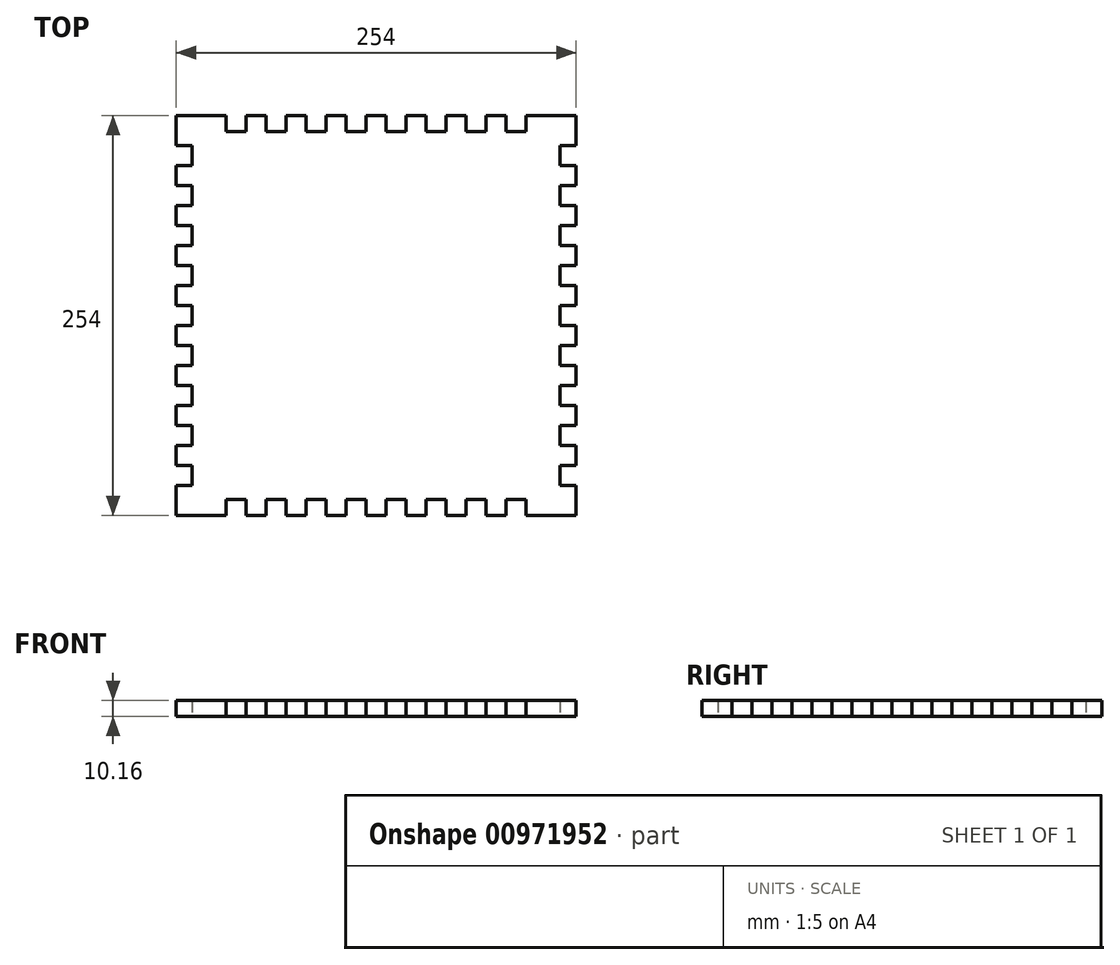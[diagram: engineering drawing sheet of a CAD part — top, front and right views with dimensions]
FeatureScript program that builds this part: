
annotation { "Feature Type Name" : "Feature", "Feature Type Description" : "" }
export const myFeature = defineFeature(function(context is Context, id is Id, definition is map)
    precondition{}
    {
        {
            var Q0;
            Q0=qCreatedBy(makeId("Top.planeOp"),FACE);
            var sketch = newSketch(context, id + "F0", { "sketchPlane" : qUnion([Q0])});
            skLineSegment(sketch, "E0.bottom", {"start": v(0, 0) * mm, "end": v(31.75, 0) * mm});
            skLineSegment(sketch, "E0.left", {"start": v(0, 0) * mm, "end": v(0, -19.05) * mm});
            skLineSegment(sketch, "E1", {"start": v(0, -19.05) * mm, "end": v(10.16, -19.05) * mm});
            skLineSegment(sketch, "E2", {"start": v(10.16, -19.05) * mm, "end": v(10.16, -31.75) * mm});
            skLineSegment(sketch, "E3", {"start": v(10.16, -31.75) * mm, "end": v(0, -31.75) * mm});
            skLineSegment(sketch, "E4", {"start": v(0, -31.75) * mm, "end": v(0, -44.45) * mm});
            skLineSegment(sketch, "E5", {"start": v(0, -44.45) * mm, "end": v(10.16, -44.45) * mm});
            skLineSegment(sketch, "E6", {"start": v(10.16, -44.45) * mm, "end": v(10.16, -57.15) * mm});
            skLineSegment(sketch, "E7", {"start": v(10.16, -57.15) * mm, "end": v(0, -57.15) * mm});
            skLineSegment(sketch, "E8", {"start": v(0, -57.15) * mm, "end": v(0, -69.85) * mm});
            skLineSegment(sketch, "E9", {"start": v(0, -69.85) * mm, "end": v(10.16, -69.85) * mm});
            skLineSegment(sketch, "E10", {"start": v(10.16, -69.85) * mm, "end": v(10.16, -82.55) * mm});
            skLineSegment(sketch, "E11", {"start": v(10.16, -82.55) * mm, "end": v(0, -82.55) * mm});
            skLineSegment(sketch, "E12.trimOffspring", {"start": v(0, -82.55) * mm, "end": v(0, -95.25) * mm});
            skLineSegment(sketch, "E13", {"start": v(0, -95.25) * mm, "end": v(10.16, -95.25) * mm});
            skLineSegment(sketch, "E14", {"start": v(10.16, -95.25) * mm, "end": v(10.16, -107.95) * mm});
            skLineSegment(sketch, "E15", {"start": v(10.16, -107.95) * mm, "end": v(0, -107.95) * mm});
            skLineSegment(sketch, "E16", {"start": v(0, -107.95) * mm, "end": v(0, -120.65) * mm});
            skLineSegment(sketch, "E17", {"start": v(0, -120.65) * mm, "end": v(10.16, -120.65) * mm});
            skLineSegment(sketch, "E18", {"start": v(10.16, -120.65) * mm, "end": v(10.16, -133.35) * mm});
            skLineSegment(sketch, "E19", {"start": v(10.16, -133.35) * mm, "end": v(0, -133.35) * mm});
            skLineSegment(sketch, "E20", {"start": v(0, -133.35) * mm, "end": v(0, -146.05) * mm});
            skLineSegment(sketch, "E21", {"start": v(0, -146.05) * mm, "end": v(10.16, -146.05) * mm});
            skLineSegment(sketch, "E22", {"start": v(10.16, -146.05) * mm, "end": v(10.16, -158.75) * mm});
            skLineSegment(sketch, "E23", {"start": v(10.16, -158.75) * mm, "end": v(0, -158.75) * mm});
            skLineSegment(sketch, "E24.trimOffspring", {"start": v(0, -158.75) * mm, "end": v(0, -171.45) * mm});
            skLineSegment(sketch, "E25", {"start": v(0, -171.45) * mm, "end": v(10.16, -171.45) * mm});
            skLineSegment(sketch, "E26", {"start": v(10.16, -171.45) * mm, "end": v(10.16, -184.15) * mm});
            skLineSegment(sketch, "E27", {"start": v(10.16, -184.15) * mm, "end": v(0, -184.15) * mm});
            skLineSegment(sketch, "E28", {"start": v(0, -184.15) * mm, "end": v(0, -196.85) * mm});
            skLineSegment(sketch, "E29", {"start": v(0, -196.85) * mm, "end": v(10.16, -196.85) * mm});
            skLineSegment(sketch, "E30", {"start": v(10.16, -196.85) * mm, "end": v(10.16, -209.55) * mm});
            skLineSegment(sketch, "E31", {"start": v(10.16, -209.55) * mm, "end": v(0, -209.55) * mm});
            skLineSegment(sketch, "E32", {"start": v(0, -209.55) * mm, "end": v(0, -222.25) * mm});
            skLineSegment(sketch, "E33", {"start": v(0, -222.25) * mm, "end": v(10.16, -222.25) * mm});
            skLineSegment(sketch, "E34", {"start": v(10.16, -222.25) * mm, "end": v(10.16, -234.95) * mm});
            skLineSegment(sketch, "E35", {"start": v(10.16, -234.95) * mm, "end": v(0, -234.95) * mm});
            skLineSegment(sketch, "E36.trimOffspring", {"start": v(0, -234.95) * mm, "end": v(0, -254) * mm});
            skLineSegment(sketch, "E37", {"start": v(31.75, 0) * mm, "end": v(31.75, -10.16) * mm});
            skLineSegment(sketch, "E38", {"start": v(31.75, -10.16) * mm, "end": v(44.45, -10.16) * mm});
            skLineSegment(sketch, "E39", {"start": v(44.45, -10.16) * mm, "end": v(44.45, 0) * mm});
            skLineSegment(sketch, "E40", {"start": v(44.45, 0) * mm, "end": v(57.15, 0) * mm});
            skLineSegment(sketch, "E41", {"start": v(57.15, 0) * mm, "end": v(57.15, -10.16) * mm});
            skLineSegment(sketch, "E42", {"start": v(57.15, -10.16) * mm, "end": v(69.85, -10.16) * mm});
            skLineSegment(sketch, "E43", {"start": v(69.85, -10.16) * mm, "end": v(69.85, 0) * mm});
            skLineSegment(sketch, "E44", {"start": v(69.85, 0) * mm, "end": v(82.55, 0) * mm});
            skLineSegment(sketch, "E45", {"start": v(82.55, 0) * mm, "end": v(82.55, -10.16) * mm});
            skLineSegment(sketch, "E46", {"start": v(82.55, -10.16) * mm, "end": v(95.25, -10.16) * mm});
            skLineSegment(sketch, "E47", {"start": v(95.25, -10.16) * mm, "end": v(95.25, 0) * mm});
            skLineSegment(sketch, "E48.trimOffspring", {"start": v(95.25, 0) * mm, "end": v(107.95, 0) * mm});
            skLineSegment(sketch, "E49", {"start": v(107.95, 0) * mm, "end": v(107.95, -10.16) * mm});
            skLineSegment(sketch, "E50", {"start": v(107.95, -10.16) * mm, "end": v(120.65, -10.16) * mm});
            skLineSegment(sketch, "E51", {"start": v(120.65, -10.16) * mm, "end": v(120.65, 0) * mm});
            skLineSegment(sketch, "E52", {"start": v(120.65, 0) * mm, "end": v(133.35, 0) * mm});
            skLineSegment(sketch, "E53", {"start": v(133.35, 0) * mm, "end": v(133.35, -10.16) * mm});
            skLineSegment(sketch, "E54", {"start": v(133.35, -10.16) * mm, "end": v(146.05, -10.16) * mm});
            skLineSegment(sketch, "E55", {"start": v(146.05, -10.16) * mm, "end": v(146.05, 0) * mm});
            skLineSegment(sketch, "E56", {"start": v(146.05, 0) * mm, "end": v(158.75, 0) * mm});
            skLineSegment(sketch, "E57", {"start": v(158.75, 0) * mm, "end": v(158.75, -10.16) * mm});
            skLineSegment(sketch, "E58", {"start": v(158.75, -10.16) * mm, "end": v(171.45, -10.16) * mm});
            skLineSegment(sketch, "E59", {"start": v(171.45, -10.16) * mm, "end": v(171.45, 0) * mm});
            skLineSegment(sketch, "E60.trimOffspring", {"start": v(171.45, 0) * mm, "end": v(184.15, 0) * mm});
            skLineSegment(sketch, "E61", {"start": v(184.15, 0) * mm, "end": v(184.15, -10.16) * mm});
            skLineSegment(sketch, "E62", {"start": v(184.15, -10.16) * mm, "end": v(196.85, -10.16) * mm});
            skLineSegment(sketch, "E63", {"start": v(196.85, -10.16) * mm, "end": v(196.85, 0) * mm});
            skLineSegment(sketch, "E64", {"start": v(196.85, 0) * mm, "end": v(209.55, 0) * mm});
            skLineSegment(sketch, "E65", {"start": v(209.55, 0) * mm, "end": v(209.55, -10.16) * mm});
            skLineSegment(sketch, "E66", {"start": v(209.55, -10.16) * mm, "end": v(222.25, -10.16) * mm});
            skLineSegment(sketch, "E67", {"start": v(222.25, -10.16) * mm, "end": v(222.25, 0) * mm});
            skLineSegment(sketch, "E68.trimOffspring", {"start": v(222.25, 0) * mm, "end": v(254, 0) * mm});
            skLineSegment(sketch, "E69", {"start": v(127, 0) * mm, "end": v(127, -28.6) * mm, "construction": true});
            skLineSegment(sketch, "E70", {"start": v(10.16, -127) * mm, "end": v(33.98, -127) * mm, "construction": true});
            skLineSegment(sketch, "E71.MirrorCS", {"start": v(254, -133.35) * mm, "end": v(254, -146.05) * mm});
            skLineSegment(sketch, "E72.MirrorCS", {"start": v(254, -82.55) * mm, "end": v(254, -95.25) * mm});
            skLineSegment(sketch, "E73.MirrorCS", {"start": v(254, -184.15) * mm, "end": v(254, -196.85) * mm});
            skLineSegment(sketch, "E74.MirrorCS", {"start": v(254, -158.75) * mm, "end": v(254, -171.45) * mm});
            skLineSegment(sketch, "E75.MirrorCS", {"start": v(254, -31.75) * mm, "end": v(254, -44.45) * mm});
            skLineSegment(sketch, "E76.MirrorCS", {"start": v(254, -209.55) * mm, "end": v(254, -222.25) * mm});
            skLineSegment(sketch, "E77.MirrorCS", {"start": v(254, -57.15) * mm, "end": v(254, -69.85) * mm});
            skLineSegment(sketch, "E78.MirrorCS", {"start": v(254, -107.95) * mm, "end": v(254, -120.65) * mm});
            skLineSegment(sketch, "E79.MirrorCS", {"start": v(243.84, -209.55) * mm, "end": v(254, -209.55) * mm});
            skLineSegment(sketch, "E80.MirrorCS", {"start": v(254, -69.85) * mm, "end": v(243.84, -69.85) * mm});
            skLineSegment(sketch, "E81.MirrorCS", {"start": v(254, -19.05) * mm, "end": v(243.84, -19.05) * mm});
            skLineSegment(sketch, "E82.MirrorCS", {"start": v(243.84, -133.35) * mm, "end": v(254, -133.35) * mm});
            skLineSegment(sketch, "E83.MirrorCS", {"start": v(243.84, -107.95) * mm, "end": v(254, -107.95) * mm});
            skLineSegment(sketch, "E84.MirrorCS", {"start": v(254, -44.45) * mm, "end": v(243.84, -44.45) * mm});
            skLineSegment(sketch, "E85.MirrorCS", {"start": v(243.84, -184.15) * mm, "end": v(254, -184.15) * mm});
            skLineSegment(sketch, "E86.MirrorCS", {"start": v(243.84, -158.75) * mm, "end": v(254, -158.75) * mm});
            skLineSegment(sketch, "E87.MirrorCS", {"start": v(254, -222.25) * mm, "end": v(243.84, -222.25) * mm});
            skLineSegment(sketch, "E88.MirrorCS", {"start": v(254, -196.85) * mm, "end": v(243.84, -196.85) * mm});
            skLineSegment(sketch, "E89.MirrorCS", {"start": v(254, -171.45) * mm, "end": v(243.84, -171.45) * mm});
            skLineSegment(sketch, "E90.MirrorCS", {"start": v(243.84, -31.75) * mm, "end": v(254, -31.75) * mm});
            skLineSegment(sketch, "E91.MirrorCS", {"start": v(254, -146.05) * mm, "end": v(243.84, -146.05) * mm});
            skLineSegment(sketch, "E92.MirrorCS", {"start": v(254, -120.65) * mm, "end": v(243.84, -120.65) * mm});
            skLineSegment(sketch, "E93.MirrorCS", {"start": v(243.84, -82.55) * mm, "end": v(254, -82.55) * mm});
            skLineSegment(sketch, "E94.MirrorCS", {"start": v(243.84, -95.25) * mm, "end": v(243.84, -107.95) * mm});
            skLineSegment(sketch, "E95.MirrorCS", {"start": v(243.84, -234.95) * mm, "end": v(254, -234.95) * mm});
            skLineSegment(sketch, "E96.MirrorCS", {"start": v(243.84, -57.15) * mm, "end": v(254, -57.15) * mm});
            skLineSegment(sketch, "E97.MirrorCS", {"start": v(243.84, -19.05) * mm, "end": v(243.84, -31.75) * mm});
            skLineSegment(sketch, "E98.MirrorCS", {"start": v(243.84, -196.85) * mm, "end": v(243.84, -209.55) * mm});
            skLineSegment(sketch, "E99.MirrorCS", {"start": v(243.84, -146.05) * mm, "end": v(243.84, -158.75) * mm});
            skLineSegment(sketch, "E100.MirrorCS", {"start": v(254, -95.25) * mm, "end": v(243.84, -95.25) * mm});
            skLineSegment(sketch, "E101.MirrorCS", {"start": v(243.84, -69.85) * mm, "end": v(243.84, -82.55) * mm});
            skLineSegment(sketch, "E102.MirrorCS", {"start": v(243.84, -222.25) * mm, "end": v(243.84, -234.95) * mm});
            skLineSegment(sketch, "E103.MirrorCS", {"start": v(243.84, -171.45) * mm, "end": v(243.84, -184.15) * mm});
            skLineSegment(sketch, "E104.MirrorCS", {"start": v(243.84, -120.65) * mm, "end": v(243.84, -133.35) * mm});
            skLineSegment(sketch, "E105.MirrorCS", {"start": v(243.84, -44.45) * mm, "end": v(243.84, -57.15) * mm});
            skLineSegment(sketch, "E106.MirrorCS", {"start": v(254, -234.95) * mm, "end": v(254, -254) * mm});
            skLineSegment(sketch, "E107.MirrorCS", {"start": v(254, 0) * mm, "end": v(254, -19.05) * mm});
            skLineSegment(sketch, "E108.MirrorCS", {"start": v(69.85, -254) * mm, "end": v(82.55, -254) * mm});
            skLineSegment(sketch, "E109.MirrorCS", {"start": v(120.65, -254) * mm, "end": v(133.35, -254) * mm});
            skLineSegment(sketch, "E110.MirrorCS", {"start": v(171.45, -254) * mm, "end": v(184.15, -254) * mm});
            skLineSegment(sketch, "E111.MirrorCS", {"start": v(196.85, -254) * mm, "end": v(209.55, -254) * mm});
            skLineSegment(sketch, "E112.MirrorCS", {"start": v(95.25, -254) * mm, "end": v(107.95, -254) * mm});
            skLineSegment(sketch, "E113.MirrorCS", {"start": v(44.45, -254) * mm, "end": v(57.15, -254) * mm});
            skLineSegment(sketch, "E114.MirrorCS", {"start": v(146.05, -254) * mm, "end": v(158.75, -254) * mm});
            skLineSegment(sketch, "E115.MirrorCS", {"start": v(158.75, -254) * mm, "end": v(158.75, -243.84) * mm});
            skLineSegment(sketch, "E116.MirrorCS", {"start": v(31.75, -254) * mm, "end": v(31.75, -243.84) * mm});
            skLineSegment(sketch, "E117.MirrorCS", {"start": v(95.25, -243.84) * mm, "end": v(95.25, -254) * mm});
            skLineSegment(sketch, "E118.MirrorCS", {"start": v(209.55, -243.84) * mm, "end": v(222.25, -243.84) * mm});
            skLineSegment(sketch, "E119.MirrorCS", {"start": v(82.55, -254) * mm, "end": v(82.55, -243.84) * mm});
            skLineSegment(sketch, "E120.MirrorCS", {"start": v(158.75, -243.84) * mm, "end": v(171.45, -243.84) * mm});
            skLineSegment(sketch, "E121.MirrorCS", {"start": v(31.75, -243.84) * mm, "end": v(44.45, -243.84) * mm});
            skLineSegment(sketch, "E122.MirrorCS", {"start": v(196.85, -243.84) * mm, "end": v(196.85, -254) * mm});
            skLineSegment(sketch, "E123.MirrorCS", {"start": v(57.15, -254) * mm, "end": v(57.15, -243.84) * mm});
            skLineSegment(sketch, "E124.MirrorCS", {"start": v(120.65, -243.84) * mm, "end": v(120.65, -254) * mm});
            skLineSegment(sketch, "E125.MirrorCS", {"start": v(146.05, -243.84) * mm, "end": v(146.05, -254) * mm});
            skLineSegment(sketch, "E126.MirrorCS", {"start": v(57.15, -243.84) * mm, "end": v(69.85, -243.84) * mm});
            skLineSegment(sketch, "E127.MirrorCS", {"start": v(107.95, -243.84) * mm, "end": v(120.65, -243.84) * mm});
            skLineSegment(sketch, "E128.MirrorCS", {"start": v(69.85, -243.84) * mm, "end": v(69.85, -254) * mm});
            skLineSegment(sketch, "E129.MirrorCS", {"start": v(82.55, -243.84) * mm, "end": v(95.25, -243.84) * mm});
            skLineSegment(sketch, "E130.MirrorCS", {"start": v(184.15, -243.84) * mm, "end": v(196.85, -243.84) * mm});
            skLineSegment(sketch, "E131.MirrorCS", {"start": v(44.45, -243.84) * mm, "end": v(44.45, -254) * mm});
            skLineSegment(sketch, "E132.MirrorCS", {"start": v(171.45, -243.84) * mm, "end": v(171.45, -254) * mm});
            skLineSegment(sketch, "E133.MirrorCS", {"start": v(184.15, -254) * mm, "end": v(184.15, -243.84) * mm});
            skLineSegment(sketch, "E134.MirrorCS", {"start": v(133.35, -254) * mm, "end": v(133.35, -243.84) * mm});
            skLineSegment(sketch, "E135.MirrorCS", {"start": v(222.25, -243.84) * mm, "end": v(222.25, -254) * mm});
            skLineSegment(sketch, "E136.MirrorCS", {"start": v(107.95, -254) * mm, "end": v(107.95, -243.84) * mm});
            skLineSegment(sketch, "E137.MirrorCS", {"start": v(209.55, -254) * mm, "end": v(209.55, -243.84) * mm});
            skLineSegment(sketch, "E138.MirrorCS", {"start": v(133.35, -243.84) * mm, "end": v(146.05, -243.84) * mm});
            skLineSegment(sketch, "E139.MirrorCS", {"start": v(222.25, -254) * mm, "end": v(254, -254) * mm});
            skLineSegment(sketch, "E140.MirrorCS", {"start": v(0, -254) * mm, "end": v(31.75, -254) * mm});
            skSolve(sketch);
        }
        {
            var Q0;
            Q0=makeQuery(id+"F0.imprint","IMPRINT",FACE,{"disambiguationData":[TD([[makeQuery(id+"F0.imprint","IMPRINT",EDGE,{"derivedFrom":sQuery(id+"F0.wireOp",EDGE,"E0.left")}),1.0]])]});
            extrude(context, id + "F1", {"entities" : qUnion([Q0]), "depth" : 10.16 * mm, "offsetDistance" : 25.4 * mm});
        }
    });
